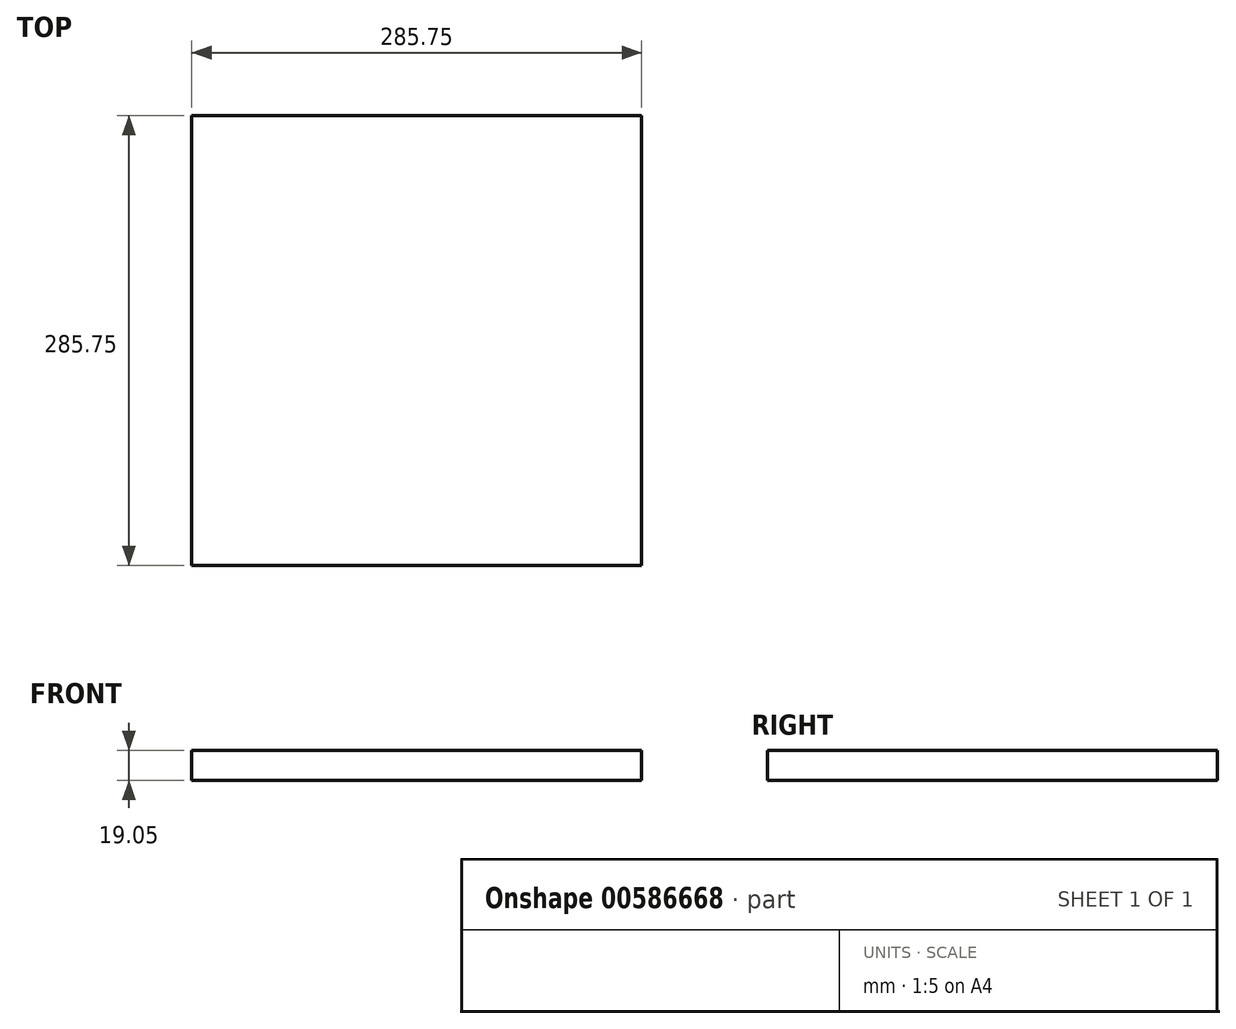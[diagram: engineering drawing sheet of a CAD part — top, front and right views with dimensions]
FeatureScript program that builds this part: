
annotation { "Feature Type Name" : "Feature", "Feature Type Description" : "" }
export const myFeature = defineFeature(function(context is Context, id is Id, definition is map)
    precondition{}
    {
        {
            var Q0;
            Q0=qCreatedBy(makeId("Top.planeOp"),FACE);
            var sketch = newSketch(context, id + "F0", { "sketchPlane" : qUnion([Q0])});
            skLineSegment(sketch, "E0.bottom", {"start": v(139.8, 149.91) * mm, "end": v(-145.94, 149.91) * mm});
            skLineSegment(sketch, "E0.top", {"start": v(139.8, -135.84) * mm, "end": v(-145.94, -135.84) * mm});
            skLineSegment(sketch, "E0.left", {"start": v(139.8, 149.91) * mm, "end": v(139.8, -135.84) * mm});
            skLineSegment(sketch, "E0.right", {"start": v(-145.94, 149.91) * mm, "end": v(-145.94, -135.84) * mm});
            skSolve(sketch);
        }
        {
            var Q0;
            Q0 = qSketchRegion(id + "F0", true);
            extrude(context, id + "F1", {"entities" : qUnion([Q0]), "depth" : 19.05 * mm, "offsetDistance" : 25.4 * mm});
        }
    });
